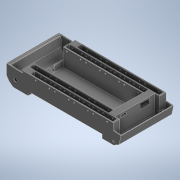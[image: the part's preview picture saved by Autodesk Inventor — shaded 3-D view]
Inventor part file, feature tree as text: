
AUTODESK INVENTOR PART (.ipt)
format: ipt  version: 2022 (Build 260153000, 153)  size: 1,005,568 bytes
history: native  units: mm
features: sketch x37, extrude x36, chamfer x6, fillet x2, mirror x1
ambient origin geometry x8: Origin, YZ Plane, XZ Plane, XY Plane, X Axis, Y Axis, Z Axis, Center Point
bodies: Solid1 (feature_tree)
feature tree (82):
  extrude  "Extrusion1"  Depth=247.347mm
  extrude  "Extrusion2"  Depth=38.0143mm TaperAngle=0.0deg
  extrude  "Extrusion3"  Depth=2.0mm
  extrude  "Extrusion4"  Depth=12.5mm
  extrude  "Extrusion5"  Depth=1.0mm
  chamfer  "Chamfer1"  [1 undecoded]
  extrude  "Extrusion6"  Depth=2.0mm
  extrude  "Extrusion7"  TaperAngle=0.0deg  [1 undecoded]
  extrude  "Extrusion8"  Depth=245.847mm TaperAngle=45.0deg
  fillet  "Fillet1"  Radius=25.5mm
  fillet  "Fillet2"  Radius=3.0mm
  sketch  "Sketch9"  dims[d23=13.8mm]
  extrude  "Extrusion9"  Depth=48.0mm
  extrude  "Extrusion10"  Depth=5.0mm
  extrude  "Extrusion12"  Depth=7.5mm
  extrude  "Extrusion13"  Depth=1.0mm
  extrude  "Extrusion14"  Depth=2.0mm
  extrude  "Extrusion15"  Depth=35.0mm
  extrude  "Extrusion16"  Depth=11.65mm
  extrude  "Extrusion17"  Depth=6.0mm
  extrude  "Extrusion18"  Depth=6.0mm
  extrude  "Extrusion19"  Depth=10.0mm
  extrude  "Extrusion20"  Depth=10.0mm
  extrude  "Extrusion21"  Depth=10.0mm
  extrude  "Extrusion22"  Depth=2.0mm TaperAngle=0.0deg
  chamfer  "Chamfer2"  Distance=2.0mm
  extrude  "Extrusion23"  Depth=38.5mm TaperAngle=0.0deg
  mirror  "Mirror1"
  extrude  "Extrusion24"  Depth=1.0mm
  extrude  "Extrusion25"  Depth=10.0mm
  extrude  "Extrusion26"  Depth=6.0mm
  extrude  "Extrusion27"  Depth=10.0mm
  extrude  "Extrusion28"  Depth=2.2mm
  extrude  "Extrusion31"  Depth=2.0mm
  chamfer  "Chamfer3"  Distance=2.2mm
  extrude  "Extrusion32"  Depth=2.0mm
  extrude  "Extrusion33"  Depth=2.0mm
  chamfer  "Chamfer4"  Distance=11.95mm
  chamfer  "Chamfer5"  Distance=30.05mm
  extrude  "Extrusion34"  Depth=2.0mm
  extrude  "Extrusion35"  Depth=2.0mm
  extrude  "Extrusion36"  Depth=2.0mm
  extrude  "Extrusion37"  Depth=2.0mm
  extrude  "Extrusion38"  Depth=10.0mm
  extrude  "Extrusion39"  Depth=2.0mm
  chamfer  "Chamfer6"  Distance=21.0mm
  sketch  "Sketch1"  dims[d0=115.0mm d1=247.347mm]
  sketch  "Sketch2"  dims[d2=115.0mm d3=38.0143mm d4=0.0mm]
  sketch  "Sketch3"  dims[d5=3.5mm d9=2.0mm]
  sketch  "Sketch4"  dims[d12=8.0mm d13=12.5mm]
  sketch  "Sketch5"  dims[d14=6.981317mm d17=1.0mm]
  sketch  "Sketch6"  dims[d20=16.4144mm]
  sketch  "Sketch7"  dims[d21=13.8mm]
  sketch  "Sketch8"  dims[d22=30.0deg]
  sketch  "Sketch10"  dims[d24=19.1mm]
  sketch  "Sketch11"  dims[d26=17.14mm]
  sketch  "Sketch13"  dims[d27=1.5mm]
  sketch  "Sketch14"  dims[d28=2.5mm d29=0.0mm d30=0.0mm]
  sketch  "Sketch15"  dims[d31=2.0mm d32=2.0mm]
  sketch  "Sketch16"  dims[d33=34.5143mm d34=0.0mm d35=0.0mm d36=0.0mm]
  sketch  "Sketch17"  dims[d37=0.0mm d38=0.0mm d39=245.847mm d40=12.197mm d41=45.0deg d42=25.5mm d43=3.0mm]
  sketch  "Sketch18"  dims[d44=0.0mm d45=0.0mm d46=48.0mm]
  sketch  "Sketch19"  dims[d47=5.0mm d48=5.0mm]
  sketch  "Sketch20"  dims[d49=12.535mm d50=0.0mm d51=7.5mm]
  sketch  "Sketch22"  dims[d52=0.0mm d53=0.0mm d54=1.0mm]
  sketch  "Sketch23"  dims[d55=2.0mm d56=37.0mm]
  sketch  "Sketch24"  dims[d59=15.0mm d60=35.0mm]
  sketch  "Sketch25"  dims[d61=2.2mm d62=11.65mm]
  sketch  "Sketch29"  dims[d66=18.4mm d68=6.0mm]
  sketch  "Sketch30"  dims[d69=5.0mm d70=6.0mm]
  sketch  "Sketch31"  dims[d71=10.0mm d73=21.0mm]
  sketch  "Sketch32"  dims[d74=2.2mm d77=10.0mm]
  sketch  "Sketch33"  dims[d78=2.0mm d79=10.0mm]
  sketch  "Sketch38"  dims[d80=2.0mm d81=38.5mm d82=0.0mm]
  sketch  "Sketch39"  dims[d83=5.15mm d84=2.0mm d85=0.0mm]
  sketch  "Sketch40"  dims[d95=14.0mm d96=0.0mm d102=38.5mm d103=0.0mm]
  sketch  "Sketch41"  dims[d104=1.0mm d105=7.0mm]
  sketch  "Sketch42"  dims[d106=1.0mm d109=10.0mm]
  sketch  "Sketch43"  dims[d110=37.05mm d111=6.0mm]
  sketch  "Sketch45"  dims[d112=10.0mm d113=2.2mm]
  sketch  "Sketch47"  dims[d116=2.2mm d119=2.2mm]
  sketch  "Sketch48"  dims[d122=2.2mm d125=2.2mm d128=2.2mm d131=11.95mm d132=30.05mm d133=11.95mm d134=30.05mm d135=11.95mm d136=30.05mm d137=7.0mm d142=2.0mm d143=10.0mm d144=6.0mm d145=21.0mm d146=30.05mm d147=11.95mm d148=30.05mm d149=11.95mm d150=30.05mm d151=11.95mm d152=30.05mm d153=7.0mm d154=38.5mm d155=0.0mm d156=7.0mm d167=7.0mm d168=30.05mm d169=18.4mm d170=41.0mm d171=2.2mm d172=21.0mm d173=21.0mm d174=21.0mm d175=21.0mm d176=21.0mm d177=21.0mm d178=21.0mm d179=15.0mm d180=14.0mm d181=0.0mm d184=2.2mm d185=2.2mm d186=2.2mm d187=2.2mm d188=2.2mm d189=2.2mm d190=2.2mm d191=2.2mm d192=1.0mm d193=10.0mm d194=13.75mm d195=2.3mm d196=30.05mm d197=9.05mm d198=2.3mm d199=30.05mm d200=9.05mm d201=2.3mm d202=2.3mm d203=2.3mm d204=2.3mm d205=2.3mm d206=2.3mm d207=2.3mm d208=2.3mm d209=2.3mm d210=2.3mm d211=2.3mm d212=2.3mm d213=2.3mm d214=2.3mm d215=7.0mm d216=5.0mm d217=1.6mm d218=10.0mm d219=0.0mm d220=10.0mm d221=0.0mm d222=5.0mm d223=7.0mm d224=18.4mm d225=18.4mm d226=9.05mm d227=30.05mm d228=2.3mm d229=11.95mm d230=2.3mm d231=2.3mm d232=2.3mm d233=14.0mm d234=0.0mm d235=7.0mm d236=3.0mm d237=38.5mm d238=0.0mm d239=38.5mm d240=0.0mm d241=15.0mm d242=6.0mm d243=2.5mm d244=0.0mm d245=0.0mm d246=1.5mm d247=2.0mm d248=12.0mm d249=0.0mm d250=5.0mm d251=1.224mm d252=45.0deg d253=0.0mm d254=0.0mm d260=21.0mm d261=10.5mm d263=10.5mm d264=4.0mm d265=3.0mm d266=4.0mm d267=3.0mm d268=3.0mm d269=3.0mm d270=10.0mm d271=0.0mm d272=1.3mm d273=1.3mm d274=0.0mm d275=0.0mm d276=12.0mm d277=18.797mm d278=0.0mm d279=12.0mm d280=6.2mm d281=0.0mm d282=3.503mm d283=0.0mm d293=5.0mm d294=0.0mm d295=21.979mm d296=5.0mm d297=45.0deg d298=2.0mm d299=2.0mm d300=5.0mm d301=0.0mm d302=5.0mm d303=0.0mm d304=8.0mm d305=5.0mm d306=45.0deg d307=8.0mm d308=5.0mm d309=45.0deg d310=2.3mm d311=2.3mm d312=2.3mm d313=2.3mm d314=2.3mm d315=2.3mm d316=4.4mm d317=111.0mm d318=0.0mm d319=95.0mm d320=0.0mm d321=4.0mm d322=10.0mm d323=3.5mm d324=0.0mm d325=19.5mm d326=12.4mm d327=15.0mm d328=0.0mm d330=25.0mm d331=0.0mm d332=2.0mm d333=2.35mm d334=0.0mm d335=0.018mm d336=2.0mm d337=45.0deg]
note: 2 required parameter values undecoded (feature->parameter linkage not recoverable at this tier; creation-order binding heuristic only, values carry confidence <= 0.55)
